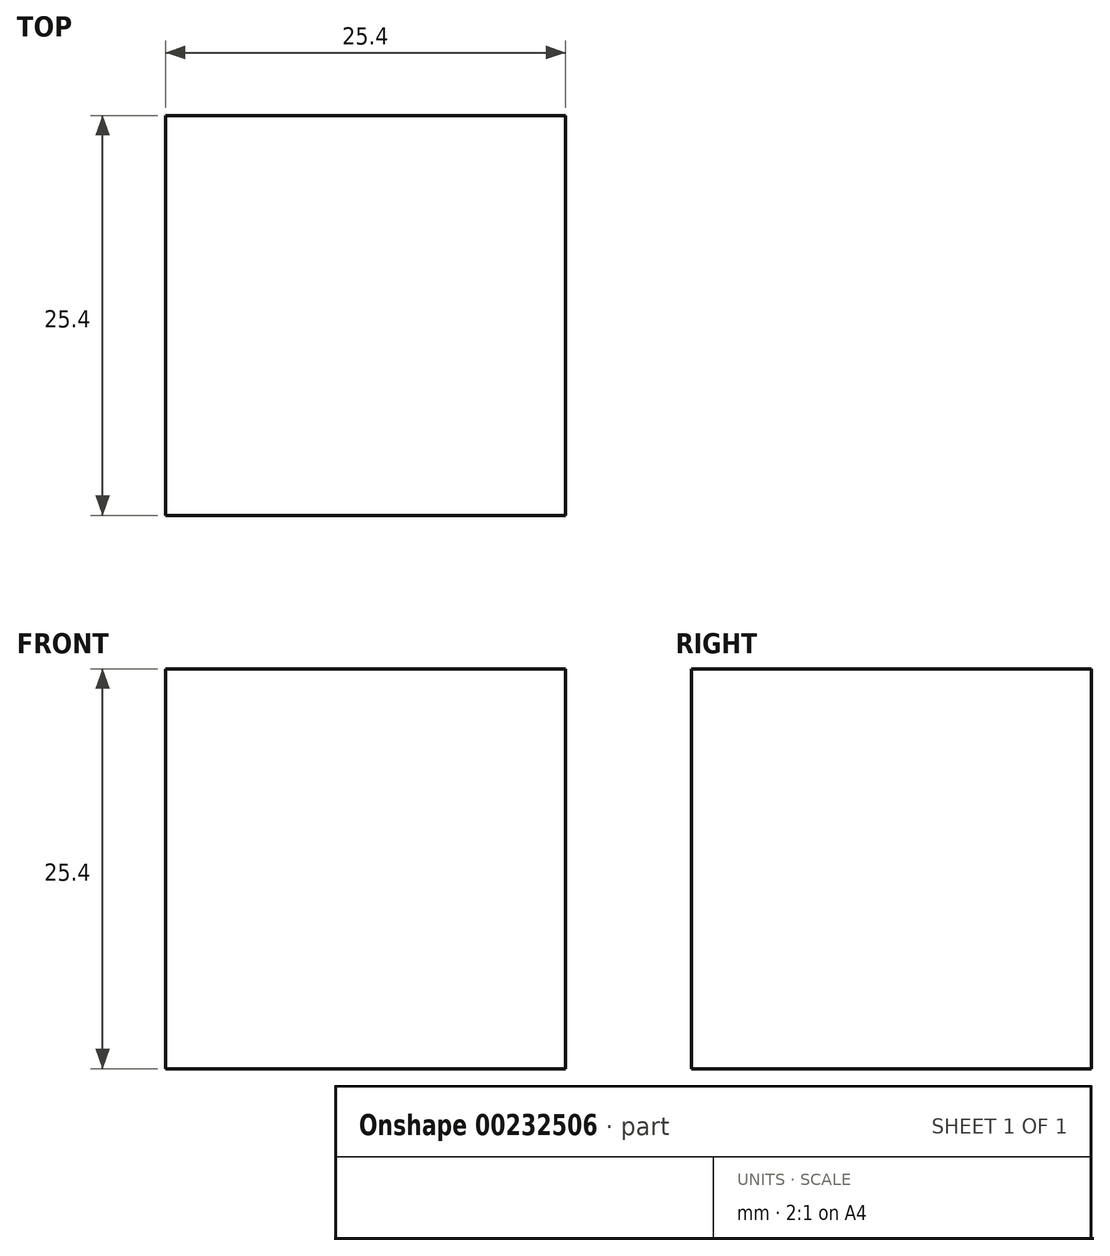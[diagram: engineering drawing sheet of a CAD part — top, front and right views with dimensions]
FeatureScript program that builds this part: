
annotation { "Feature Type Name" : "Feature", "Feature Type Description" : "" }
export const myFeature = defineFeature(function(context is Context, id is Id, definition is map)
    precondition{}
    {
        {
            var Q0;
            Q0=qCreatedBy(makeId("Front.planeOp"),FACE);
            var sketch = newSketch(context, id + "F0", { "sketchPlane" : qUnion([Q0])});
            skLineSegment(sketch, "E0.bottom", {"start": v(-30.66, 49.4) * mm, "end": v(-5.26, 49.4) * mm});
            skLineSegment(sketch, "E0.top", {"start": v(-30.66, 24) * mm, "end": v(-5.26, 24) * mm});
            skLineSegment(sketch, "E0.left", {"start": v(-30.66, 49.4) * mm, "end": v(-30.66, 24) * mm});
            skLineSegment(sketch, "E0.right", {"start": v(-5.26, 49.4) * mm, "end": v(-5.26, 24) * mm});
            skSolve(sketch);
        }
        {
            var Q0;
            Q0=makeQuery(id+"F0.imprint","IMPRINT",FACE,{"disambiguationData":[TD([[makeQuery(id+"F0.imprint","IMPRINT",EDGE,{"derivedFrom":sQuery(id+"F0.wireOp",EDGE,"E0.bottom")}),-1.0]])]});
            extrude(context, id + "F1", {"entities" : qUnion([Q0]), "depth" : 25.4 * mm});
        }
    });
